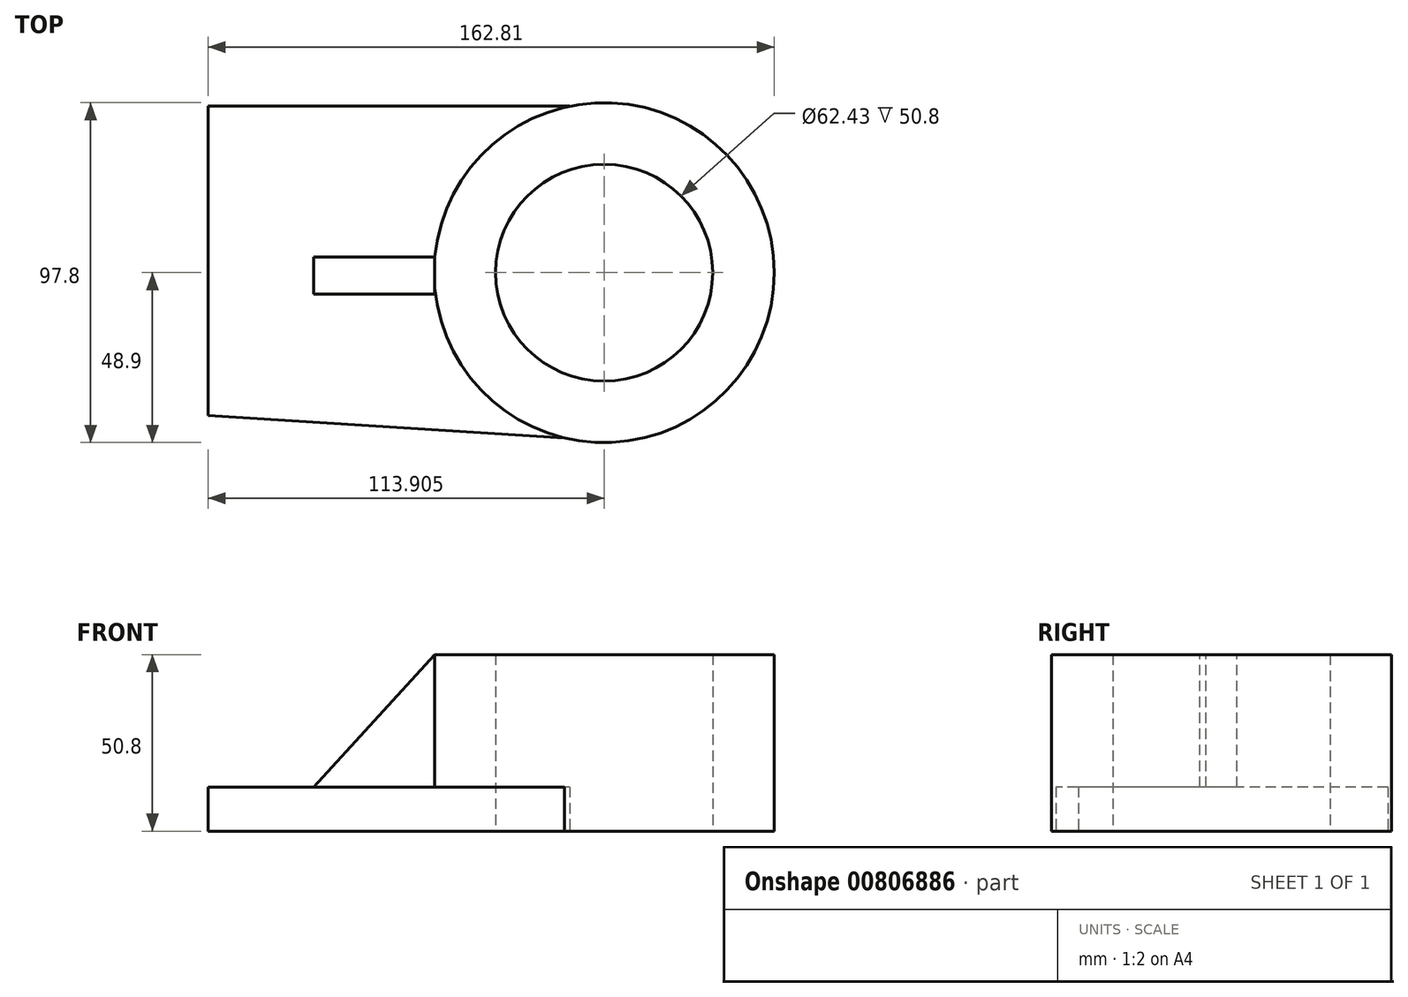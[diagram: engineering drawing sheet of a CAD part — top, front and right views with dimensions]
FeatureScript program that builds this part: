
annotation { "Feature Type Name" : "Feature", "Feature Type Description" : "" }
export const myFeature = defineFeature(function(context is Context, id is Id, definition is map)
    precondition{}
    {
        {
            var Q0;
            Q0=qCreatedBy(makeId("Top.planeOp"),FACE);
            var sketch = newSketch(context, id + "F0", { "sketchPlane" : qUnion([Q0])});
            skCircle(sketch, "E0", {"center": v(38.66, 0) * mm, "radius": 48.9 * mm});
            skCircle(sketch, "E1", {"center": v(38.66, 0) * mm, "radius": 31.22 * mm});
            skLineSegment(sketch, "E2", {"start": v(28.78, 47.9) * mm, "end": v(-75.24, 47.9) * mm});
            skLineSegment(sketch, "E3", {"start": v(-75.24, 47.9) * mm, "end": v(-75.24, -41.14) * mm});
            skLineSegment(sketch, "E4", {"start": v(-75.24, -41.14) * mm, "end": v(27.24, -47.55) * mm});
            skSolve(sketch);
        }
        {
            var Q0;
            Q0=makeQuery(id+"F0.imprint","IMPRINT",FACE,{"disambiguationData":[TD([[makeQuery(id+"F0.imprint","IMPRINT",EDGE,{"derivedFrom":sQuery(id+"F0.wireOp",EDGE,"E0")}),1.0]])]});
            extrude(context, id + "F1", {"entities" : qUnion([Q0]), "depth" : 50.8 * mm, "offsetDistance" : 25.4 * mm});
        }
        {
            var Q0;
            {var subQ0=sQuery(id+"F0.wireOp",EDGE,"E2");Q0=makeQuery(id+"F0.imprint","IMPRINT",FACE,{"disambiguationData":[TD([[makeQuery(id+"F0.imprint","IMPRINT",EDGE,{"derivedFrom":subQ0}),1.0]])]});}
            extrude(context, id + "F2", {"entities" : qUnion([Q0]), "operationType" : NewBodyOperationType.ADD, "depth" : 12.7 * mm, "offsetDistance" : 25.4 * mm});
        }
        {
            var Q0;
            Q0=makeQuery(id+"F1.opExtrude","CAP_FACE",FACE,{"disambiguationData":[OSD([sQuery(id+"F0.wireOp",EDGE,"E0"),sQuery(id+"F0.wireOp",EDGE,"E1")])],"isStart":false});
            var sketch = newSketch(context, id + "F3", { "sketchPlane" : qUnion([Q0])});
            skLineSegment(sketch, "E5.bottom", {"start": v(-10.04, 4.44) * mm, "end": v(-44.9, 4.44) * mm});
            skLineSegment(sketch, "E5.top", {"start": v(-10.04, -6.23) * mm, "end": v(-44.9, -6.23) * mm});
            skLineSegment(sketch, "E5.left", {"start": v(-10.04, 4.44) * mm, "end": v(-10.04, -6.23) * mm});
            skLineSegment(sketch, "E5.right", {"start": v(-44.9, 4.44) * mm, "end": v(-44.9, -6.23) * mm});
            skSolve(sketch);
        }
        {
            var Q0;
            {var subQ4=sQuery(id+"F3.wireOp",EDGE,"E5.bottom");Q0=makeQuery(id+"F3.imprint","IMPRINT",FACE,{"disambiguationData":[TD([[makeQuery(id+"F3.imprint","IMPRINT",EDGE,{"derivedFrom":subQ4}),1.0]])]});}
            extrude(context, id + "F4", {"entities" : qUnion([Q0]), "operationType" : NewBodyOperationType.ADD, "oppositeDirection" : true, "depth" : 38.86 * mm, "offsetDistance" : 25.4 * mm});
        }
        {
            var Q0;
            Q0=makeQuery(id+"F4.opExtrude","SWEPT_FACE",FACE,{"disambiguationData":[OSD([sQuery(id+"F3.wireOp",EDGE,"E5.top")])]});
            var sketch = newSketch(context, id + "F5", { "sketchPlane" : qUnion([Q0])});
            skLineSegment(sketch, "E6", {"start": v(-44.9, 12.7) * mm, "end": v(-10.04, 50.8) * mm});
            skLineSegment(sketch, "E7", {"start": v(-10.04, 50.8) * mm, "end": v(-44.9, 50.8) * mm});
            skLineSegment(sketch, "E8", {"start": v(-44.9, 50.8) * mm, "end": v(-44.9, 12.7) * mm});
            skSolve(sketch);
        }
        {
            var Q0;
            Q0=makeQuery(id+"F5.imprint","IMPRINT",FACE,{"disambiguationData":[TD([[makeQuery(id+"F5.imprint","IMPRINT",EDGE,{"derivedFrom":sQuery(id+"F5.wireOp",EDGE,"E6")}),1.0]])]});
            extrude(context, id + "F6", {"entities" : qUnion([Q0]), "operationType" : NewBodyOperationType.REMOVE, "oppositeDirection" : true, "depth" : 177.8 * mm, "offsetDistance" : 25.4 * mm});
        }
    });
